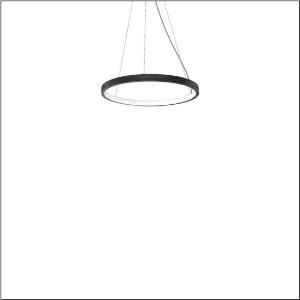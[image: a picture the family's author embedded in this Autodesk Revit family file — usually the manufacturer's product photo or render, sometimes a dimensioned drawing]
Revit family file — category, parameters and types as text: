
# Revit family: silica_r__21_ring-i_5pjbi1d3104a_e1bb
name_source: partatom
category: Lighting Fixtures
units: mm (PartAtom-declared; Revit-internal decimal feet)

## family parameters
Cut with Voids When Loaded = No
Host = Face
Light Source = No
Part Type = Normal
Room Calculation Point = No
Round Connector Dimension = Use Diameter
Shared = No

## types (1)
- Silica® 21 Ring-I (1 x LED, 3510 lm, 60 W, 4000K)
    Apparent Load = 60 VA
    CIE Flux Codes = 22 48 76 50 101
    Color Rendering = 80
    Color Temperature = 4000K
    Default Elevation = 1800 mm
    Description = Silica® 21 Ring-I, suspended luminaire, of PMMA, frosted, light emission: inner ring side luminous distribution, primary light characteristic: symmetric, installation type: suspended mounting, LED, rated luminous flux: 3.510lm, luminous efficacy: 59lm/W, light colour: 840, colour temperature: 4000K, with terminal, 5-pole, mains connection: 230V, AC/DC, 0/50..60Hz, rated input power: 60W, housing, of extruded aluminium section, jet black (RAL 9005), diameter: 610mm, ceiling canopy, jet black (RAL 9005), protection rating (lamp compartment): IP40, insulation class (complete): insulation class I (protective earthing), certification: CE, impact resistance: IK02, permissible operating ambient temperature: 0..+35°C, packaging unit: 1 piece
    Height = 48 mm  [stored 0.15748 ft]
    Lamp = 1 x LED
    Lamp Light Flux = 3510 lm
    Lamp Power = 60 W
    Lamp count = 1
    Length = 610 mm
    Luminous efficacy = 59 lm/W
    Manufacturer = Siteco
    ModVariant = No
    Model = 5PJBI1D3104A
    Mounting Place = Ceiling
    Mounting Type = Pendant
    Number of Poles = 1
    OnlyDefault = Yes
    Power Factor = 1
    Product Name = Silica® 21 Ring-I
    Product group = suspended luminaire
    ProductGroupID = 904
    Protection Class = Protection class I
    Protection Degree = IP 40
    RLX_Detail_Level = 1
    RLX_Emergency_Light_Flux = 0 lm
    RLX_Emergency_Type = 0
    RLX_Emergency_Type_DB = No
    RlxData = <blob elided: 12337 chars, md5=a0182f39>
    Socket = socket
    Standby Power = 0 W
    System Light Flux = 3510 lm
    System Power = 60 W
    Type Comments = Product without accessories
    Type Image = l_1258361.jpg
    URL = http://relux.com
    VarID = ---
    Voltage = 0 V
    Weight = 0.00 kg
    Width = 0 mm  [stored 0 ft]

note: [stored X ft] marks values corroborated as IEEE doubles in the binary element streams (Revit-internal decimal feet)

## geometry (parser evidence)
native form markers: Sweep x10
no freeform markers — native parametric forms only
